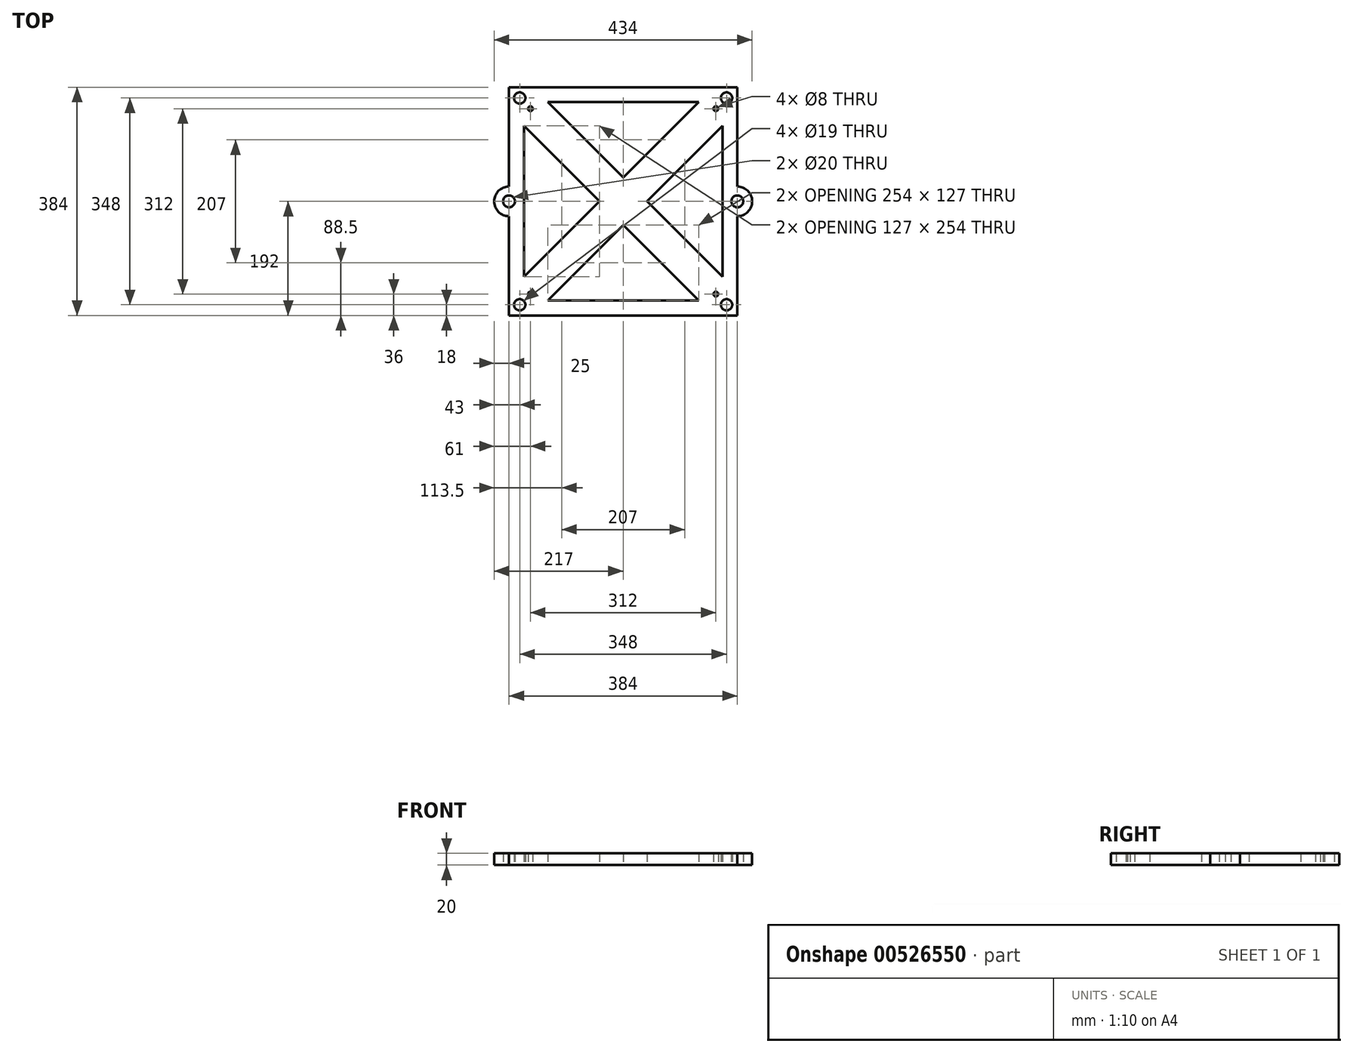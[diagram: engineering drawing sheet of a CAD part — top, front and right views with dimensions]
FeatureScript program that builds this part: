
annotation { "Feature Type Name" : "Feature", "Feature Type Description" : "" }
export const myFeature = defineFeature(function(context is Context, id is Id, definition is map)
    precondition{}
    {
        {
            var Q0;
            Q0=qCreatedBy(makeId("Top.planeOp"),FACE);
            var sketch = newSketch(context, id + "F0", { "sketchPlane" : qUnion([Q0])});
            skLineSegment(sketch, "E0", {"start": v(-167, 127) * mm, "end": v(-127, 167) * mm});
            skLineSegment(sketch, "E1", {"start": v(-127, 167) * mm, "end": v(-127, 192) * mm});
            skLineSegment(sketch, "E2", {"start": v(-127, 192) * mm, "end": v(-192, 192) * mm});
            skLineSegment(sketch, "E3", {"start": v(-192, 192) * mm, "end": v(-192, 127) * mm});
            skLineSegment(sketch, "E4", {"start": v(-192, 127) * mm, "end": v(-167, 127) * mm});
            skCircle(sketch, "E5", {"center": v(-174, 174) * mm, "radius": 9.5 * mm});
            skCircle(sketch, "E6", {"center": v(-156, 156) * mm, "radius": 4 * mm});
            skLineSegment(sketch, "E7.MirrorCS", {"start": v(167, 127) * mm, "end": v(127, 167) * mm});
            skLineSegment(sketch, "E8.MirrorCS", {"start": v(127, 167) * mm, "end": v(127, 192) * mm});
            skLineSegment(sketch, "E9.MirrorCS", {"start": v(127, 192) * mm, "end": v(192, 192) * mm});
            skLineSegment(sketch, "E10.MirrorCS", {"start": v(192, 127) * mm, "end": v(167, 127) * mm});
            skLineSegment(sketch, "E11.MirrorCS", {"start": v(192, 192) * mm, "end": v(192, 127) * mm});
            skCircle(sketch, "E12.MirrorC", {"center": v(174, 174) * mm, "radius": 9.5 * mm});
            skCircle(sketch, "E13.MirrorC", {"center": v(156, 156) * mm, "radius": 4 * mm});
            skLineSegment(sketch, "E14.MirrorCS", {"start": v(127, -167) * mm, "end": v(127, -192) * mm});
            skLineSegment(sketch, "E15.MirrorCS", {"start": v(127, -192) * mm, "end": v(192, -192) * mm});
            skCircle(sketch, "E16.MirrorC", {"center": v(174, -174) * mm, "radius": 9.5 * mm});
            skCircle(sketch, "E17.MirrorC", {"center": v(156, -156) * mm, "radius": 4 * mm});
            skLineSegment(sketch, "E18.MirrorCS", {"start": v(167, -127) * mm, "end": v(127, -167) * mm});
            skLineSegment(sketch, "E19.MirrorCS", {"start": v(-127, -192) * mm, "end": v(-192, -192) * mm});
            skLineSegment(sketch, "E20.MirrorCS", {"start": v(-192, -127) * mm, "end": v(-167, -127) * mm});
            skCircle(sketch, "E21.MirrorC", {"center": v(-174, -174) * mm, "radius": 9.5 * mm});
            skCircle(sketch, "E22.MirrorC", {"center": v(-156, -156) * mm, "radius": 4 * mm});
            skLineSegment(sketch, "E23.MirrorCS", {"start": v(-192, -192) * mm, "end": v(-192, -127) * mm});
            skLineSegment(sketch, "E24.MirrorCS", {"start": v(-127, -167) * mm, "end": v(-127, -192) * mm});
            skLineSegment(sketch, "E25.MirrorCS", {"start": v(192, -127) * mm, "end": v(167, -127) * mm});
            skLineSegment(sketch, "E26.MirrorCS", {"start": v(192, -192) * mm, "end": v(192, -127) * mm});
            skLineSegment(sketch, "E27.MirrorCS", {"start": v(-167, -127) * mm, "end": v(-127, -167) * mm});
            skLineSegment(sketch, "E28", {"start": v(-192, 127) * mm, "end": v(-192, -127) * mm});
            skLineSegment(sketch, "E29", {"start": v(-167, 127) * mm, "end": v(-167, -127) * mm});
            skLineSegment(sketch, "E30", {"start": v(-127, 167) * mm, "end": v(127, 167) * mm});
            skLineSegment(sketch, "E31", {"start": v(-127, 192) * mm, "end": v(127, 192) * mm});
            skLineSegment(sketch, "E32", {"start": v(167, 127) * mm, "end": v(167, -127) * mm});
            skLineSegment(sketch, "E33", {"start": v(192, 127) * mm, "end": v(192, -127) * mm});
            skLineSegment(sketch, "E34", {"start": v(127, -167) * mm, "end": v(-127, -167) * mm});
            skLineSegment(sketch, "E35", {"start": v(-127, -192) * mm, "end": v(127, -192) * mm});
            skLineSegment(sketch, "E36", {"start": v(-167, 127) * mm, "end": v(127, -167) * mm});
            skLineSegment(sketch, "E37", {"start": v(-127, 167) * mm, "end": v(167, -127) * mm});
            skLineSegment(sketch, "E38", {"start": v(127, 167) * mm, "end": v(-167, -127) * mm});
            skLineSegment(sketch, "E39", {"start": v(167, 127) * mm, "end": v(-127, -167) * mm});
            skArc(sketch, "E40", {"start": v(-192, 25) * mm, "mid": v(-217, 0) * mm, "end": v(-192, -25) * mm});
            skArc(sketch, "E41.MirrorCS", {"start": v(192, 25) * mm, "mid": v(217, 0) * mm, "end": v(192, -25) * mm});
            skCircle(sketch, "E42", {"center": v(-192, 0) * mm, "radius": 10 * mm});
            skCircle(sketch, "E43.MirrorC", {"center": v(192, 0) * mm, "radius": 10 * mm});
            skSolve(sketch);
        }
        {
            var Q0;
            Q0 = qSketchRegion(id + "F0", true);
            var Q1;
            {var subQ0=sQuery(id+"F0.wireOp",EDGE,"E18.MirrorCS");Q1=makeQuery(id+"F0.imprint","IMPRINT",FACE,{"disambiguationData":[TD([[makeQuery(id+"F0.imprint","IMPRINT",EDGE,{"derivedFrom":subQ0}),-1.0]])]});}
            var Q2;
            {var subQ0=sQuery(id+"F0.wireOp",EDGE,"E27.MirrorCS");Q2=makeQuery(id+"F0.imprint","IMPRINT",FACE,{"disambiguationData":[TD([[makeQuery(id+"F0.imprint","IMPRINT",EDGE,{"derivedFrom":subQ0}),1.0]])]});}
            var Q3;
            {var subQ0=sQuery(id+"F0.wireOp",EDGE,"E0");Q3=makeQuery(id+"F0.imprint","IMPRINT",FACE,{"disambiguationData":[TD([[makeQuery(id+"F0.imprint","IMPRINT",EDGE,{"derivedFrom":subQ0}),-1.0]])]});}
            var Q4;
            {var subQ0=sQuery(id+"F0.wireOp",EDGE,"E38");var subQ1=sQuery(id+"F0.wireOp",EDGE,"E36");var subQ2=makeQuery(id+"F0.imprint","INTERSECT",VERTEX,{"derivedFrom":[subQ1,subQ0]});Q4=makeQuery(id+"F0.imprint","IMPRINT",FACE,{"disambiguationData":[TD([[makeQuery(id+"F0.imprint","IMPRINT",EDGE,{"disambiguationData":[TD([[subQ2,-1.0]])],"derivedFrom":subQ1}),1.0]])]});}
            var Q5;
            {var subQ0=sQuery(id+"F0.wireOp",EDGE,"E7.MirrorCS");Q5=makeQuery(id+"F0.imprint","IMPRINT",FACE,{"disambiguationData":[TD([[makeQuery(id+"F0.imprint","IMPRINT",EDGE,{"derivedFrom":subQ0}),1.0]])]});}
            extrude(context, id + "F1", {"entities" : qUnion([Q0, Q1, Q2, Q3, Q4, Q5]), "depth" : 20 * mm, "offsetDistance" : 25 * mm});
        }
    });
